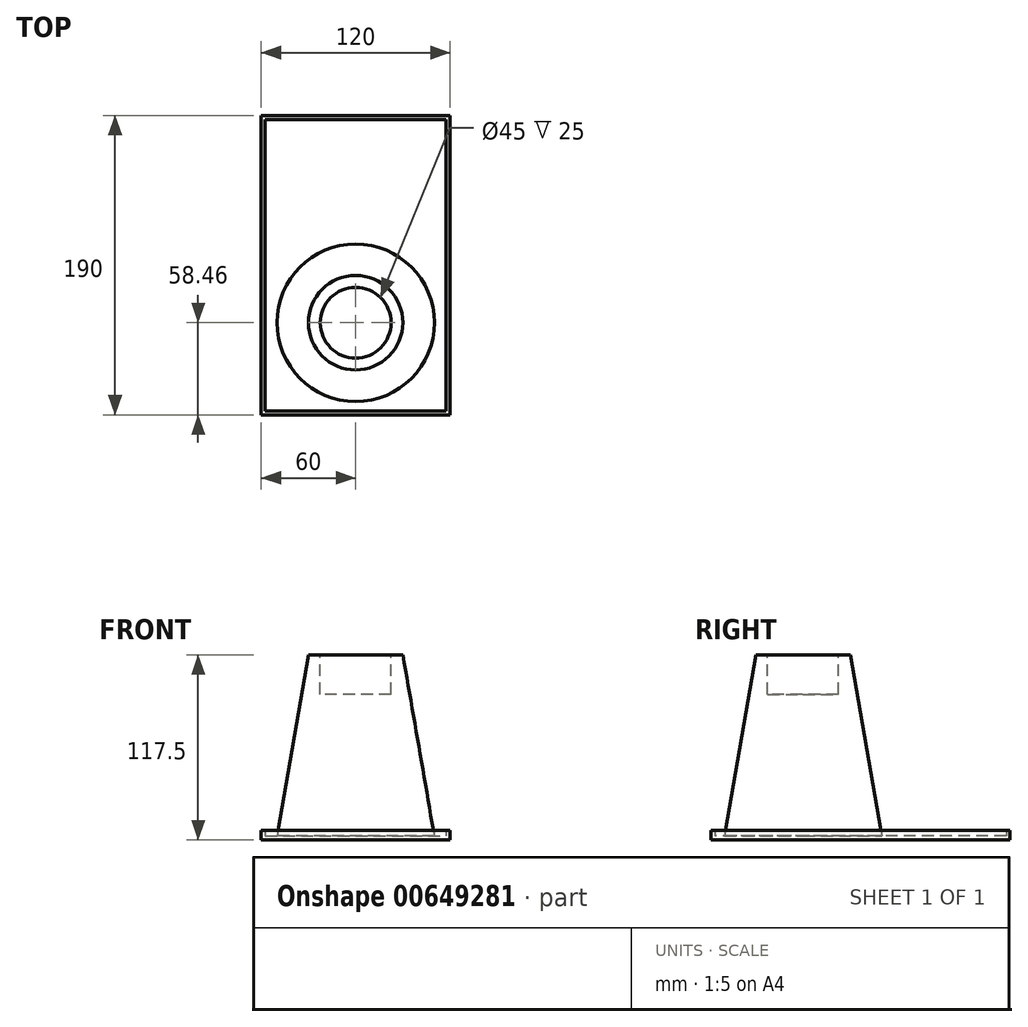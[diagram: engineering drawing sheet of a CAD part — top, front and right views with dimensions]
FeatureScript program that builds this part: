
annotation { "Feature Type Name" : "Feature", "Feature Type Description" : "" }
export const myFeature = defineFeature(function(context is Context, id is Id, definition is map)
    precondition{}
    {
        {
            var Q0;
            Q0=qCreatedBy(makeId("Top.planeOp"),FACE);
            var sketch = newSketch(context, id + "F0", { "sketchPlane" : qUnion([Q0])});
            skLineSegment(sketch, "E0.bottom", {"start": v(-60, 131.54) * mm, "end": v(60, 131.54) * mm});
            skLineSegment(sketch, "E0.top", {"start": v(-60, -58.46) * mm, "end": v(60, -58.46) * mm});
            skLineSegment(sketch, "E0.left", {"start": v(-60, 131.54) * mm, "end": v(-60, -58.46) * mm});
            skLineSegment(sketch, "E0.right", {"start": v(60, 131.54) * mm, "end": v(60, -58.46) * mm});
            skSolve(sketch);
        }
        {
            var Q0;
            Q0 = qSketchRegion(id + "F0", true);
            extrude(context, id + "F1", {"entities" : qUnion([Q0]), "depth" : 6 * mm, "offsetDistance" : 25 * mm});
        }
        {
            var Q0;
            Q0=makeQuery(id+"F1.opExtrude","CAP_FACE",FACE,{"disambiguationData":[OSD([sQuery(id+"F0.wireOp",EDGE,"E0.bottom"),sQuery(id+"F0.wireOp",EDGE,"E0.top"),sQuery(id+"F0.wireOp",EDGE,"E0.left"),sQuery(id+"F0.wireOp",EDGE,"E0.right")])],"isStart":false});
            shell(context, id + "F2", {"entities" : qUnion([Q0]), "thickness" : 2.5 * mm});
        }
        {
            var Q0;
            Q0=makeQuery(id+"F2.opShell","OFFSET_FACE",FACE,{"disambiguationData":[OSD([sQuery(id+"F0.wireOp",EDGE,"E0.bottom"),sQuery(id+"F0.wireOp",EDGE,"E0.top"),sQuery(id+"F0.wireOp",EDGE,"E0.left"),sQuery(id+"F0.wireOp",EDGE,"E0.right")])]});
            var sketch = newSketch(context, id + "F3", { "sketchPlane" : qUnion([Q0])});
            skCircle(sketch, "E1", {"center": v(0, 0) * mm, "radius": 50 * mm});
            skSolve(sketch);
        }
        {
            var Q0;
            Q0 = qSketchRegion(id + "F3", true);
            extrude(context, id + "F4", {"entities" : qUnion([Q0]), "operationType" : NewBodyOperationType.ADD, "depth" : 115 * mm, "offsetDistance" : 25 * mm});
        }
        {
            var Q0;
            Q0=makeQuery(id+"F4.opExtrude","CAP_EDGE",EDGE,{"disambiguationData":[OSD([sQuery(id+"F3.wireOp",EDGE,"E1")])],"isStart":false});
            chamfer(context, id + "F5", {"entities" : qUnion([Q0]), "chamferType" : ChamferType.TWO_OFFSETS, "width1" : 20 * mm, "oppositeDirection" : false, "width2" : 115 * mm, "tangentPropagation" : true});
        }
        {
            var Q0;
            Q0=makeQuery(id+"F4.opExtrude","CAP_FACE",FACE,{"disambiguationData":[OSD([sQuery(id+"F3.wireOp",EDGE,"E1")])],"isStart":false});
            var sketch = newSketch(context, id + "F6", { "sketchPlane" : qUnion([Q0])});
            skCircle(sketch, "E2", {"center": v(0, 0) * mm, "radius": 22.5 * mm});
            skSolve(sketch);
        }
        {
            var Q0;
            Q0 = qSketchRegion(id + "F6", true);
            extrude(context, id + "F7", {"entities" : qUnion([Q0]), "operationType" : NewBodyOperationType.REMOVE, "oppositeDirection" : true, "depth" : 25 * mm, "offsetDistance" : 25 * mm});
        }
    });
